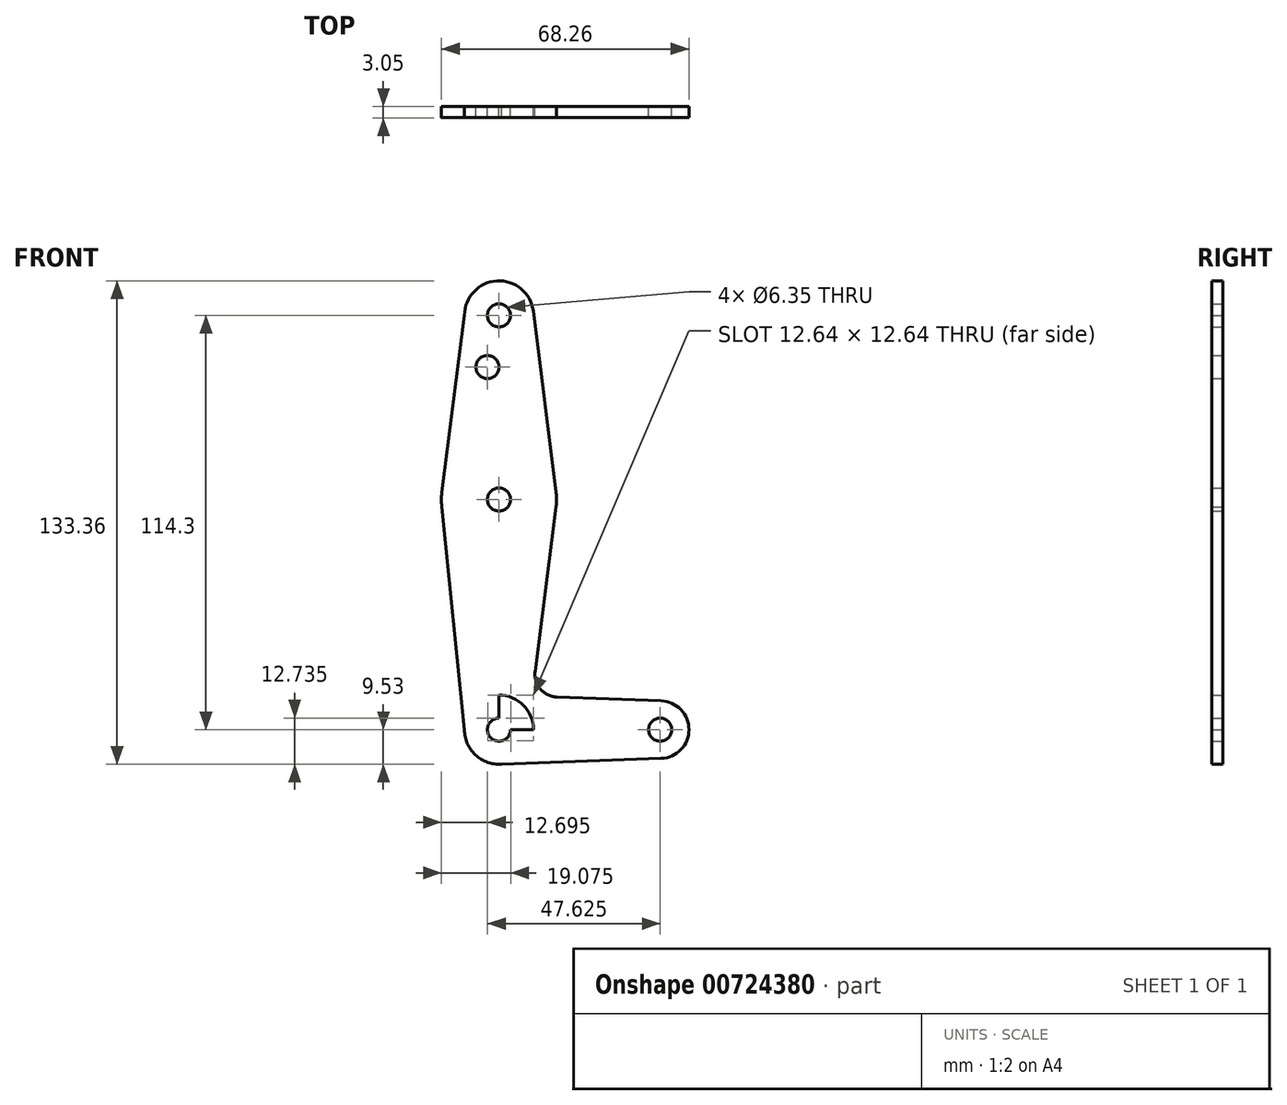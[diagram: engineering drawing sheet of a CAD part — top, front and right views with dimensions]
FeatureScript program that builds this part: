
annotation { "Feature Type Name" : "Feature", "Feature Type Description" : "" }
export const myFeature = defineFeature(function(context is Context, id is Id, definition is map)
    precondition{}
    {
        {
            var Q0;
            Q0=qCreatedBy(makeId("Front.planeOp"),FACE);
            var sketch = newSketch(context, id + "F0", { "sketchPlane" : qUnion([Q0])});
            skCircle(sketch, "E0", {"center": v(0, 114.3) * mm, "radius": 9.53 * mm});
            skCircle(sketch, "E1", {"center": v(0, 63.5) * mm, "radius": 15.88 * mm});
            skCircle(sketch, "E2", {"center": v(0, 0) * mm, "radius": 9.53 * mm});
            skCircle(sketch, "E3", {"center": v(44.45, 0) * mm, "radius": 7.94 * mm});
            skLineSegment(sketch, "E4", {"start": v(44.45, 0) * mm, "end": v(0, 0) * mm});
            skLineSegment(sketch, "E5", {"start": v(0, 0) * mm, "end": v(0, 114.3) * mm});
            skLineSegment(sketch, "E6", {"start": v(-9.52, 114.3) * mm, "end": v(-15.75, 65.5) * mm});
            skLineSegment(sketch, "E7", {"start": v(15.75, 65.5) * mm, "end": v(9.45, 115.5) * mm});
            skLineSegment(sketch, "E8", {"start": v(0, -9.53) * mm, "end": v(44.73, -7.93) * mm});
            skLineSegment(sketch, "E9", {"start": v(15.75, 61.5) * mm, "end": v(9.96, 16.1) * mm});
            skLineSegment(sketch, "E10", {"start": v(16.03, 8.95) * mm, "end": v(44.73, 7.93) * mm});
            skCircle(sketch, "E11", {"center": v(0, 114.3) * mm, "radius": 3.18 * mm});
            skLineSegment(sketch, "E12", {"start": v(-9.52, 0) * mm, "end": v(-15.75, 61.5) * mm});
            skCircle(sketch, "E13", {"center": v(0, 63.5) * mm, "radius": 3.18 * mm});
            skCircle(sketch, "E14", {"center": v(44.45, 0) * mm, "radius": 3.18 * mm});
            skCircle(sketch, "E15", {"center": v(0, 0) * mm, "radius": 3.18 * mm});
            skArc(sketch, "E16.filletArc", {"start": v(9.96, 16.1) * mm, "mid": v(11.42, 11.19) * mm, "end": v(16.03, 8.95) * mm});
            skCircle(sketch, "E17", {"center": v(-3.18, 100.03) * mm, "radius": 3.18 * mm});
            skSolve(sketch);
        }
        {
            var Q0;
            Q0 = qSketchRegion(id + "F0", true);
            extrude(context, id + "F1", {"entities" : qUnion([Q0]), "depth" : 3.05 * mm, "offsetDistance" : 25.4 * mm});
        }
    });
